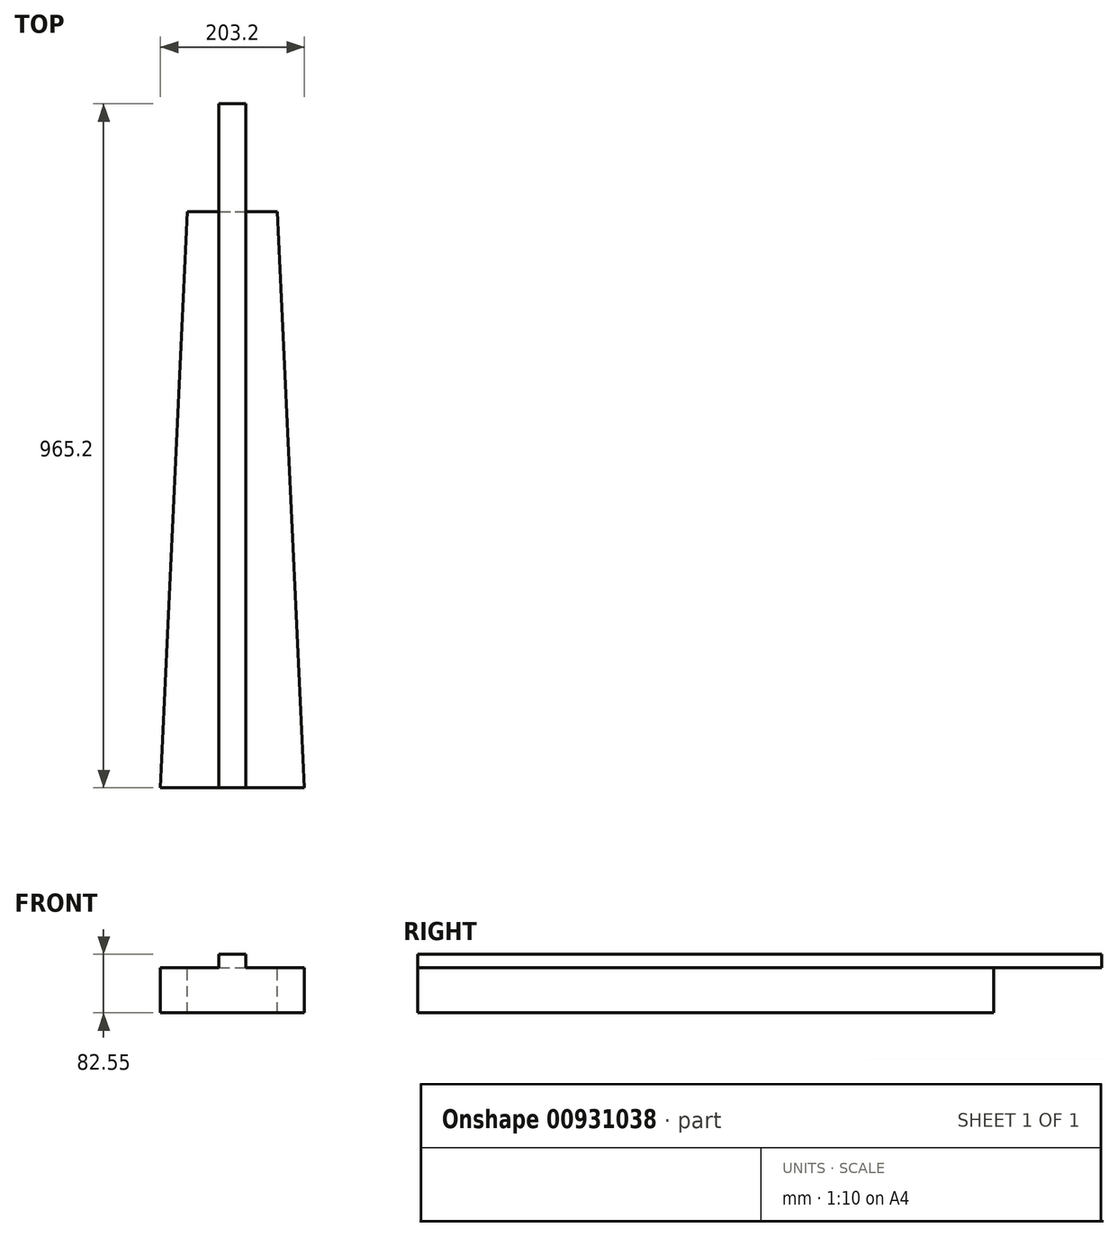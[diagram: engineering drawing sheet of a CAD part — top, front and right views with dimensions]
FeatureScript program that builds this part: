
annotation { "Feature Type Name" : "Feature", "Feature Type Description" : "" }
export const myFeature = defineFeature(function(context is Context, id is Id, definition is map)
    precondition{}
    {
        {
            var Q0;
            Q0=qCreatedBy(makeId("Top.planeOp"),FACE);
            var sketch = newSketch(context, id + "F0", { "sketchPlane" : qUnion([Q0])});
            skLineSegment(sketch, "E0.bottom", {"start": v(-19.05, 0) * mm, "end": v(19.05, 0) * mm});
            skLineSegment(sketch, "E0.top", {"start": v(-19.05, 965.2) * mm, "end": v(19.05, 965.2) * mm});
            skLineSegment(sketch, "E0.left", {"start": v(-19.05, 0) * mm, "end": v(-19.05, 965.2) * mm});
            skLineSegment(sketch, "E0.right", {"start": v(19.05, 0) * mm, "end": v(19.05, 965.2) * mm});
            skPoint(sketch, "E1", {"position": v(0, 965.2) * mm});
            skSolve(sketch);
        }
        {
            var Q0;
            Q0 = qSketchRegion(id + "F0", true);
            extrude(context, id + "F1", {"entities" : qUnion([Q0]), "depth" : 19.05 * mm, "offsetDistance" : 25.4 * mm});
        }
        {
            var Q0;
            Q0=qCreatedBy(makeId("Top.planeOp"),FACE);
            var sketch = newSketch(context, id + "F2", { "sketchPlane" : qUnion([Q0])});
            skLineSegment(sketch, "E2", {"start": v(-101.6, 0) * mm, "end": v(101.6, 0) * mm});
            skPoint(sketch, "E3", {"position": v(0, 0) * mm});
            skLineSegment(sketch, "E4", {"start": v(-63.5, 812.8) * mm, "end": v(63.5, 812.8) * mm});
            skPoint(sketch, "E5", {"position": v(0, 812.8) * mm});
            skPoint(sketch, "E6", {"position": v(6.64, 110.28) * mm});
            skLineSegment(sketch, "E7", {"start": v(-101.6, 0) * mm, "end": v(-63.5, 812.8) * mm});
            skLineSegment(sketch, "E8", {"start": v(101.6, 0) * mm, "end": v(63.5, 812.8) * mm});
            skSolve(sketch);
        }
        {
            var Q0;
            Q0 = qSketchRegion(id + "F2", true);
            extrude(context, id + "F3", {"entities" : qUnion([Q0]), "operationType" : NewBodyOperationType.ADD, "oppositeDirection" : true, "depth" : 63.5 * mm, "offsetDistance" : 25.4 * mm});
        }
    });
